# Revit family: RV3380 58
name_source: partatom
category: Luminarias
revit_build: Autodesk Revit 2015 (Build: 20140606_1530(x64)
units: mm (PartAtom-declared; Revit-internal decimal feet)

## types (10) — shared parameters
Anchura rectángulo de emisión = 170 mm  [stored 0.557743 ft]
Cambio de temperatura de color de luz atenuada = <Ninguno>
Fabricante = SECOM ILUMINACIÓN
Filtro de color = 16777215
Forma visible en renderización = No
Longitud de rectángulo de emisión = 170 mm  [stored 0.557743 ft]
Lámpara = LED Osran  Oslon SSL
Modelo = Ecodut K1
Ángulo de inclinación = 90.00°

## per-type parameters (varying)
| type | Archivo de red fotométrica | Comentarios de vataje | Descripción |
| Ecodut K1 25W | 3380 58 25 84.IES | 25W | 3380 58 25 84 |
| Ecodut K1 50W | 3380 58 50 84 .IES | 50W | 3380 58 50 84 |
| Ecodut K1 75W | 3380 58 75 84.IES | 75W | 3380 58 50 84 |
| Ecodut K1 25W Óptica asimétrica 150º | 3380 58 25 84 3407.IES | 25W | 3380 58 25 84 3407 |
| Ecodut K1 25W Óptica asimétrica street | 3380 58 75 84 3405.IES | 25W | 3380 58 25 84 3405 |
| Ecodut K1 50W Óptica asimétrica 150º | 3380 58 50 84 3407.IES | 50W | 3380 58 50 84 3407 |
| Ecodut K1 50 W Óptica simétrica 80º | 3380 58 50 84 3408.IES | 50W | 3380 58 50 84 3408 |
| Ecoduto K1 75W Óptica asimétrica street | 3380 58 75 84 3405.IES | 75W | 3380 58 50 84 3407 |
| Ecodut K1 75W Óptica simétrica 80º | 3380 58 75 84.IES | 75W | 3380 58 50 84 3408 |
| Ecodut K1 75W Óptica asimétrica 150º | 3380 58 75 84 3407.IES | 75W | 3380 58 50 84 |

note: [stored X ft] marks values corroborated as IEEE doubles in the binary element streams (Revit-internal decimal feet)
